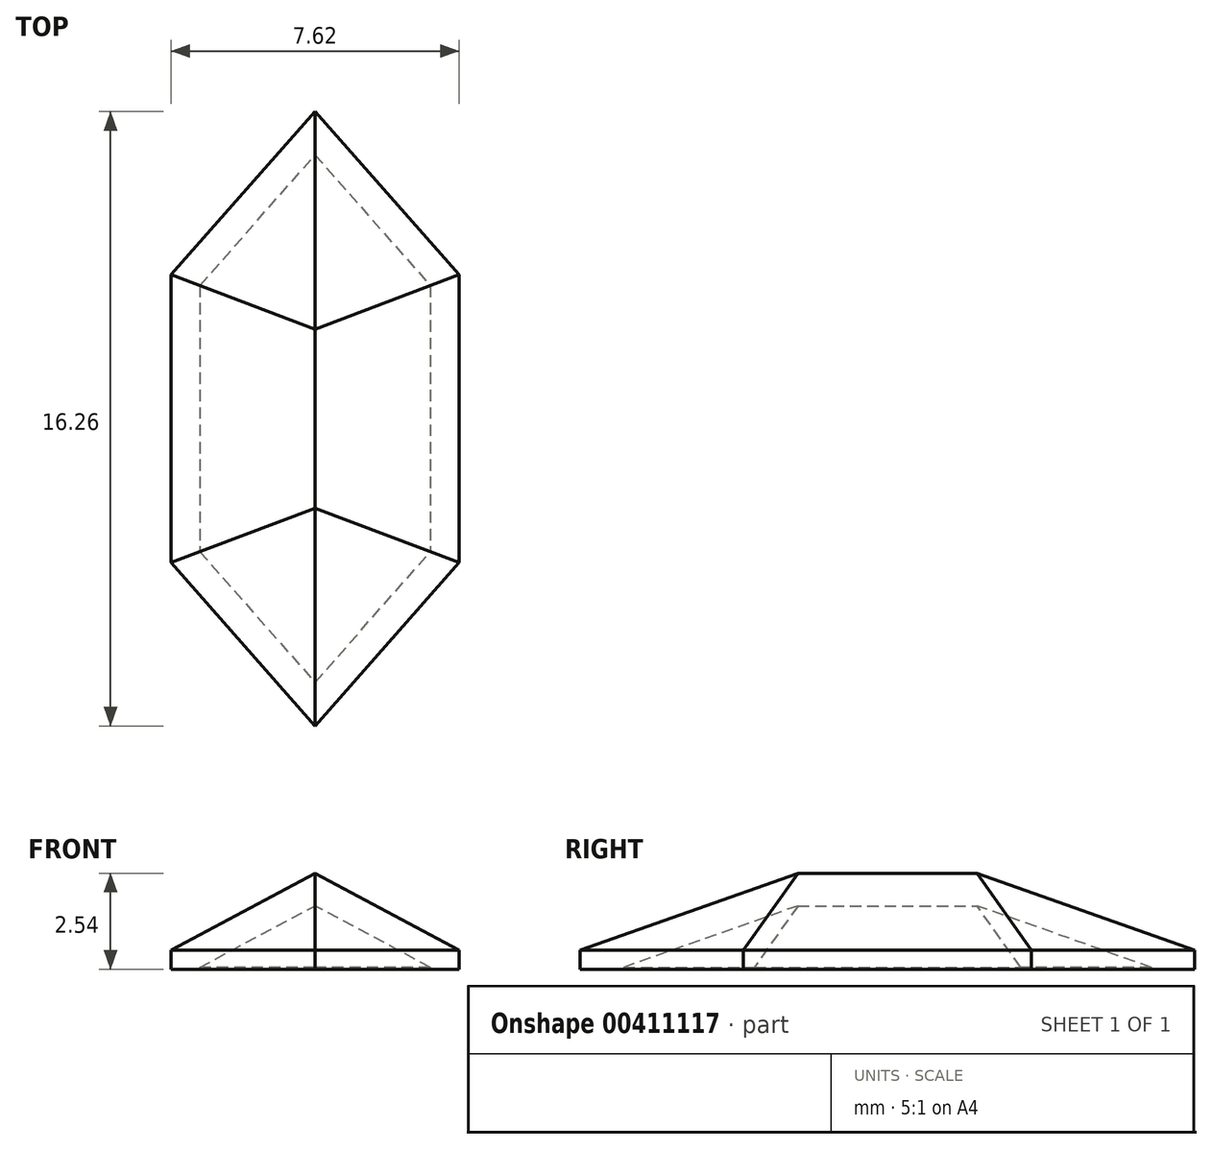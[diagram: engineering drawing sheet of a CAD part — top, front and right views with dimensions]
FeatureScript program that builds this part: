
annotation { "Feature Type Name" : "Feature", "Feature Type Description" : "" }
export const myFeature = defineFeature(function(context is Context, id is Id, definition is map)
    precondition{}
    {
        {
            var Q0;
            Q0=qCreatedBy(makeId("Top.planeOp"),FACE);
            var sketch = newSketch(context, id + "F0", { "sketchPlane" : qUnion([Q0])});
            skLineSegment(sketch, "E0.bottom", {"start": v(3.81, 3.81) * mm, "end": v(-3.81, 3.81) * mm});
            skLineSegment(sketch, "E0.top", {"start": v(3.81, -3.81) * mm, "end": v(-3.81, -3.81) * mm});
            skLineSegment(sketch, "E0.left", {"start": v(3.81, 3.81) * mm, "end": v(3.81, -3.81) * mm});
            skLineSegment(sketch, "E0.right", {"start": v(-3.81, 3.81) * mm, "end": v(-3.81, -3.81) * mm});
            skPoint(sketch, "E0.middle", {"position": v(0, 0) * mm});
            skLineSegment(sketch, "E1", {"start": v(-3.81, 3.8) * mm, "end": v(0, 8.13) * mm});
            skPoint(sketch, "E1.endSnap0", {"position": v(0, 3.81) * mm});
            skLineSegment(sketch, "E2", {"start": v(0, 8.13) * mm, "end": v(3.81, 3.8) * mm});
            skLineSegment(sketch, "E3.MirrorCS", {"start": v(0, -8.13) * mm, "end": v(3.81, -3.8) * mm});
            skLineSegment(sketch, "E4.MirrorCS", {"start": v(-3.81, -3.8) * mm, "end": v(0, -8.13) * mm});
            skSolve(sketch);
        }
        {
            var Q0;
            Q0 = qSketchRegion(id + "F0", true);
            extrude(context, id + "F1", {"entities" : qUnion([Q0]), "depth" : 2.54 * mm});
        }
        {
            var Q0;
            Q0=makeQuery(id+"F1.opExtrude","CAP_EDGE",EDGE,{"disambiguationData":[OSD([sQuery(id+"F0.wireOp",EDGE,"E0.left")])],"isStart":false});
            var Q1;
            Q1=makeQuery(id+"F1.opExtrude","CAP_EDGE",EDGE,{"disambiguationData":[OSD([sQuery(id+"F0.wireOp",EDGE,"E2")])],"isStart":false});
            var Q2;
            Q2=makeQuery(id+"F1.opExtrude","CAP_EDGE",EDGE,{"disambiguationData":[OSD([sQuery(id+"F0.wireOp",EDGE,"E4.MirrorCS")])],"isStart":false});
            var Q3;
            Q3=makeQuery(id+"F1.opExtrude","CAP_EDGE",EDGE,{"disambiguationData":[OSD([sQuery(id+"F0.wireOp",EDGE,"E0.right")])],"isStart":false});
            var Q4;
            Q4=makeQuery(id+"F1.opExtrude","CAP_EDGE",EDGE,{"disambiguationData":[OSD([sQuery(id+"F0.wireOp",EDGE,"E1")])],"isStart":false});
            var Q5;
            Q5=makeQuery(id+"F1.opExtrude","CAP_EDGE",EDGE,{"disambiguationData":[OSD([sQuery(id+"F0.wireOp",EDGE,"E3.MirrorCS")])],"isStart":false});
            chamfer(context, id + "F2", {"entities" : qUnion([Q0, Q1, Q2, Q3, Q4, Q5]), "chamferType" : ChamferType.TWO_OFFSETS, "width1" : 2.03 * mm, "oppositeDirection" : false, "width2" : 3.8 * mm, "tangentPropagation" : true});
        }
        {
            var Q0;
            Q0=makeQuery(id+"F1.opExtrude","CAP_FACE",FACE,{"disambiguationData":[OSD([sQuery(id+"F0.wireOp",EDGE,"E0.left"),sQuery(id+"F0.wireOp",EDGE,"E0.right"),sQuery(id+"F0.wireOp",EDGE,"E1"),sQuery(id+"F0.wireOp",EDGE,"E2"),sQuery(id+"F0.wireOp",EDGE,"E3.MirrorCS"),sQuery(id+"F0.wireOp",EDGE,"E4.MirrorCS")])],"isStart":true});
            shell(context, id + "F3", {"entities" : qUnion([Q0]), "thickness" : 0.76 * mm});
        }
    });
